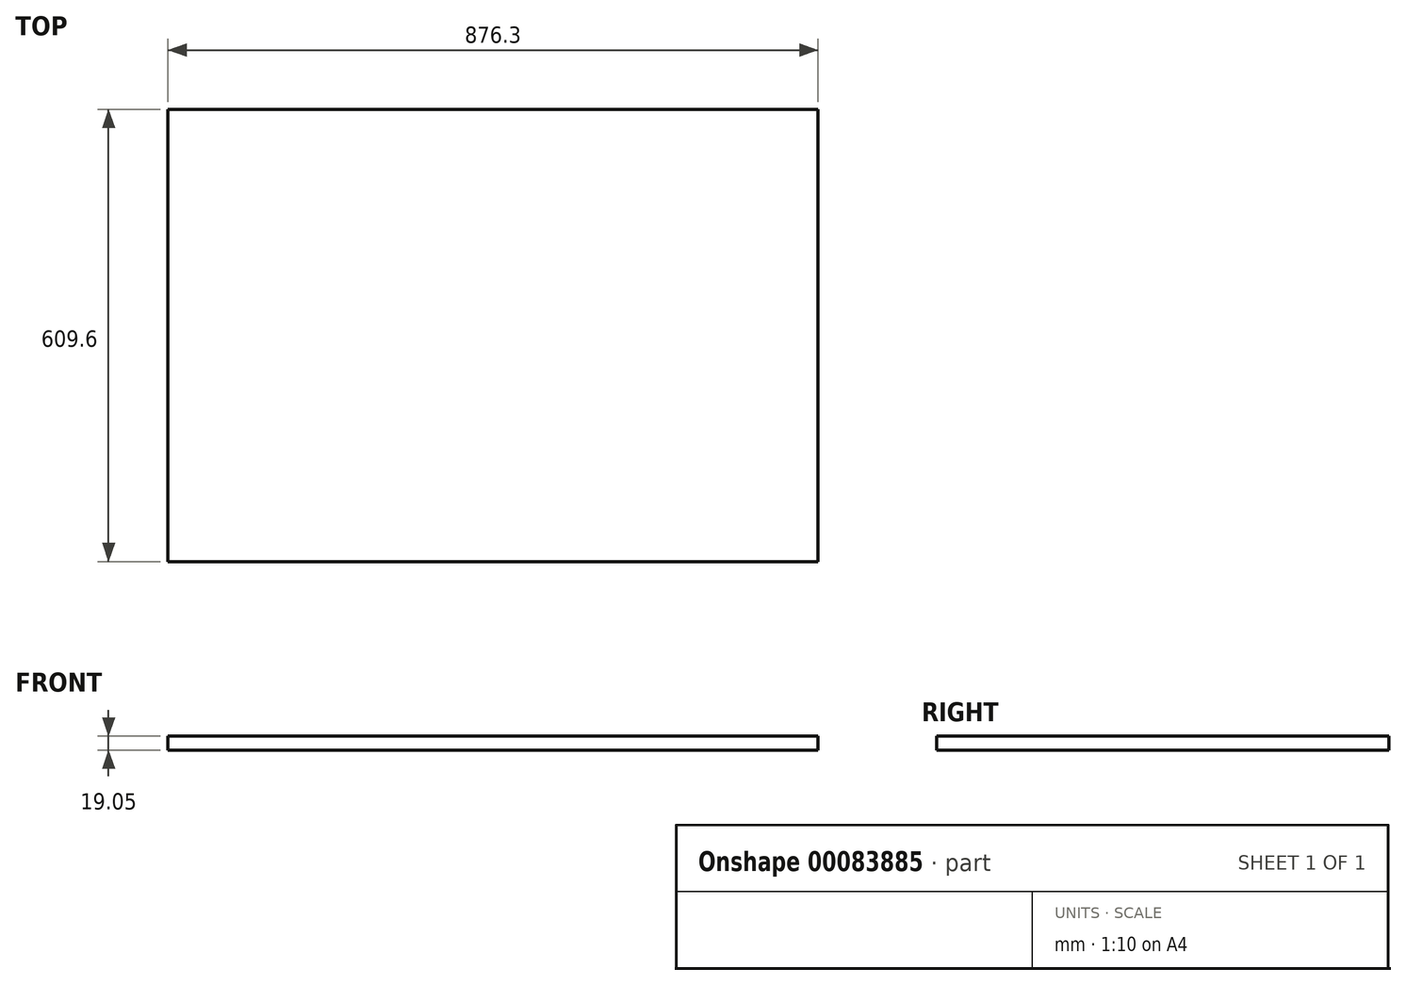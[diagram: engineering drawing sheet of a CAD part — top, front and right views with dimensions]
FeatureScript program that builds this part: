
annotation { "Feature Type Name" : "Feature", "Feature Type Description" : "" }
export const myFeature = defineFeature(function(context is Context, id is Id, definition is map)
    precondition{}
    {
        {
            var Q0;
            Q0=qCreatedBy(makeId("Top.planeOp"),FACE);
            var sketch = newSketch(context, id + "F0", { "sketchPlane" : qUnion([Q0])});
            skLineSegment(sketch, "E0.bottom", {"start": v(438.15, 304.8) * mm, "end": v(-438.15, 304.8) * mm});
            skLineSegment(sketch, "E0.top", {"start": v(438.15, -304.8) * mm, "end": v(-438.15, -304.8) * mm});
            skLineSegment(sketch, "E0.left", {"start": v(438.15, 304.8) * mm, "end": v(438.15, -304.8) * mm});
            skLineSegment(sketch, "E0.right", {"start": v(-438.15, 304.8) * mm, "end": v(-438.15, -304.8) * mm});
            skPoint(sketch, "E0.middle", {"position": v(0, 0) * mm});
            skSolve(sketch);
        }
        {
            var Q0;
            Q0=makeQuery(id+"F0.imprint","IMPRINT",FACE,{"disambiguationData":[TD([[makeQuery(id+"F0.imprint","IMPRINT",EDGE,{"derivedFrom":sQuery(id+"F0.wireOp",EDGE,"E0.bottom")}),1.0]])]});
            extrude(context, id + "F1", {"entities" : qUnion([Q0]), "depth" : 19.05 * mm});
        }
    });
